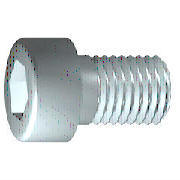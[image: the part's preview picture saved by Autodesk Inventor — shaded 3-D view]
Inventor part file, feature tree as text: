
AUTODESK INVENTOR PART (.ipt)
format: ipt  version: 2023.1 (Build 271208000, 208)  size: 204,288 bytes
history: native  units: mm (DEFAULTED — no unit token found)
features: sketch x2, extrude x1, plane x1, fillet x1
ambient origin geometry x7: Origin, YZ Plane, XY Plane, X Axis, Y Axis, Z Axis, Center Point
bodies: Solid1 (feature_tree), Body (feature_tree)
feature tree (5):
  extrude  "Slot"  Depth=3.0mm
  plane  "Work Plane1"
  fillet  "Fillet2"  Radius=3.0mm
  sketch  "Sketch1"  dims[d1=18.75mm d2=0.306825mm d3=3.0mm]
  sketch  "Sketch2"  dims[d4=1.3mm d5=60.0deg d6=3.0mm d7=3.0mm d8=2.886751mm d9=5.5mm d10=90.0deg d11=10.0mm d12=0.0mm d13=18.75mm d14=0.0mm d15=0.306725mm d16=0.306725mm d17=0.3mm d19=0.0mm d26=20.0mm d27=45.0deg d28=0.0mm d29=0.0mm d30=0.1mm]
